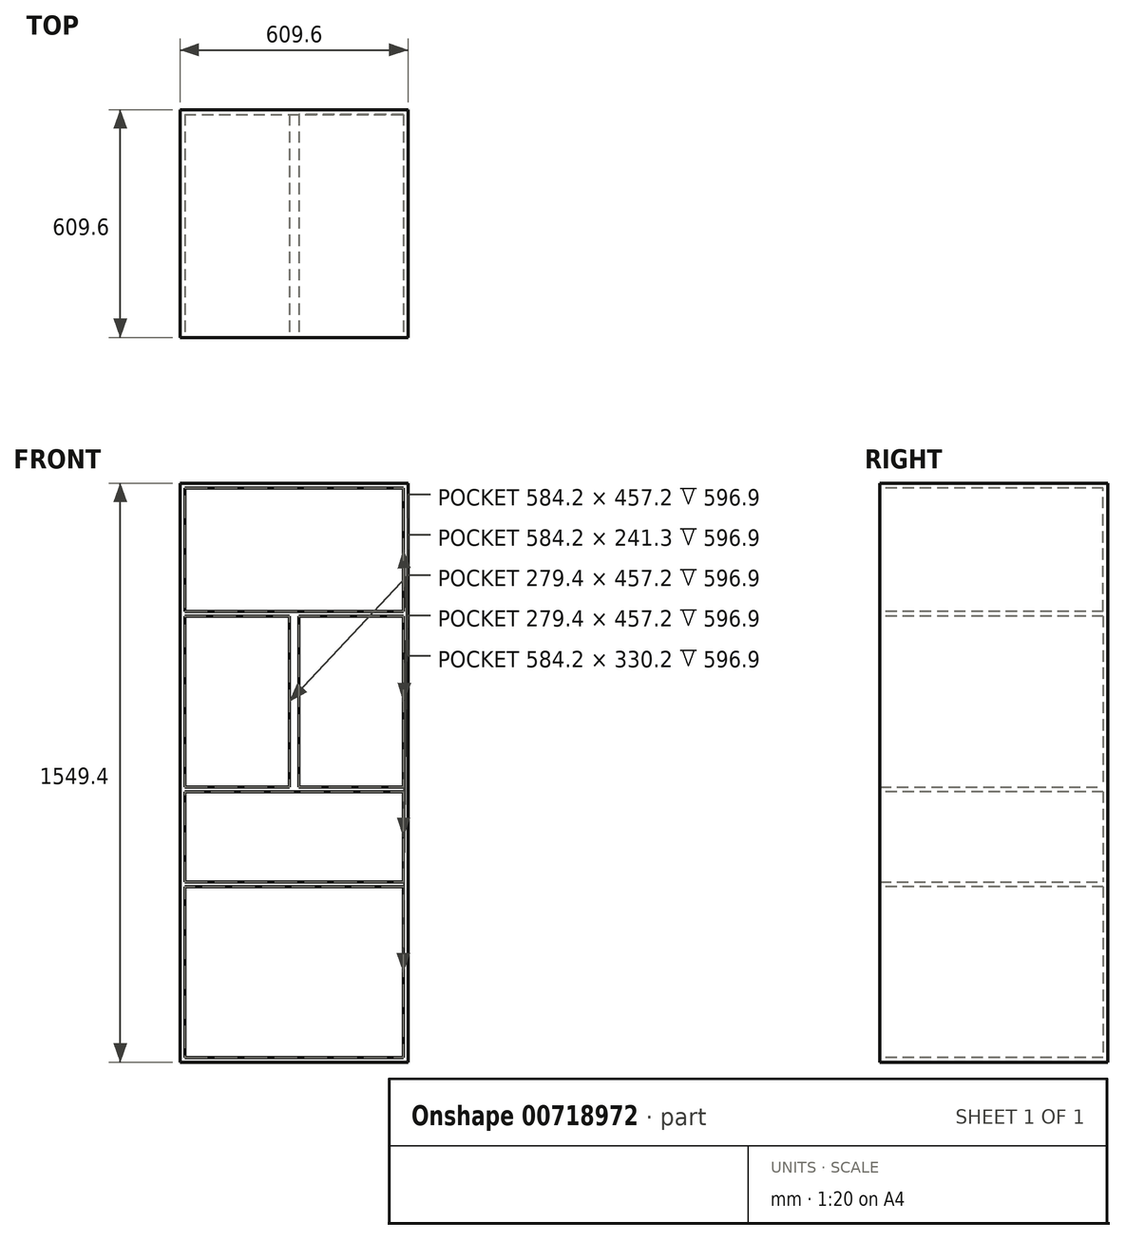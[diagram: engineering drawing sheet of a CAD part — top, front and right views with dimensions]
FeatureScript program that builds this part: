
annotation { "Feature Type Name" : "Feature", "Feature Type Description" : "" }
export const myFeature = defineFeature(function(context is Context, id is Id, definition is map)
    precondition{}
    {
        {
            var Q0;
            Q0=qCreatedBy(makeId("Top.planeOp"),FACE);
            var sketch = newSketch(context, id + "F0", { "sketchPlane" : qUnion([Q0])});
            skLineSegment(sketch, "E0.bottom", {"start": v(-300.8, 335.67) * mm, "end": v(308.8, 335.67) * mm});
            skLineSegment(sketch, "E0.top", {"start": v(-300.8, -273.93) * mm, "end": v(308.8, -273.93) * mm});
            skLineSegment(sketch, "E0.left", {"start": v(-300.8, 335.67) * mm, "end": v(-300.8, -273.93) * mm});
            skLineSegment(sketch, "E0.right", {"start": v(308.8, 335.67) * mm, "end": v(308.8, -273.93) * mm});
            skSolve(sketch);
        }
        {
            var Q0;
            Q0=makeQuery(id+"F0.imprint","IMPRINT",FACE,{"disambiguationData":[TD([[makeQuery(id+"F0.imprint","IMPRINT",EDGE,{"derivedFrom":sQuery(id+"F0.wireOp",EDGE,"E0.bottom")}),-1.0]])]});
            extrude(context, id + "F1", {"entities" : qUnion([Q0]), "depth" : 482.6 * mm, "offsetDistance" : 25.4 * mm});
        }
        {
            var Q0;
            Q0=makeQuery(id+"F1.opExtrude","SWEPT_FACE",FACE,{"disambiguationData":[OSD([sQuery(id+"F0.wireOp",EDGE,"E0.top")])]});
            shell(context, id + "F2", {"entities" : qUnion([Q0]), "thickness" : 12.7 * mm});
        }
        {
            var Q0;
            Q0=makeQuery(id+"F1.opExtrude","CAP_FACE",FACE,{"disambiguationData":[OSD([sQuery(id+"F0.wireOp",EDGE,"E0.bottom"),sQuery(id+"F0.wireOp",EDGE,"E0.top"),sQuery(id+"F0.wireOp",EDGE,"E0.left"),sQuery(id+"F0.wireOp",EDGE,"E0.right")])],"isStart":false});
            extrude(context, id + "F3", {"entities" : qUnion([Q0]), "operationType" : NewBodyOperationType.ADD, "depth" : 254 * mm, "offsetDistance" : 25.4 * mm});
        }
        {
            var Q0;
            {var subQ0=sQuery(id+"F0.wireOp",EDGE,"E0.top");Q0=makeQuery(id+"F3.boolean.opBoolean","MERGE",FACE,{"derivedFrom":[makeQuery(id+"F1.opExtrude","SWEPT_FACE",FACE,{"disambiguationData":[OSD([subQ0])]}),makeQuery(id+"F3.opExtrude","SWEPT_FACE",FACE,{"disambiguationData":[OSD([subQ0])]})]});}
            shell(context, id + "F4", {"entities" : qUnion([Q0]), "thickness" : 12.7 * mm});
        }
        {
            var Q0;
            Q0=makeQuery(id+"F3.opExtrude","CAP_FACE",FACE,{"disambiguationData":[OSD([sQuery(id+"F0.wireOp",EDGE,"E0.bottom"),sQuery(id+"F0.wireOp",EDGE,"E0.top"),sQuery(id+"F0.wireOp",EDGE,"E0.left"),sQuery(id+"F0.wireOp",EDGE,"E0.right")])],"isStart":false});
            var sketch = newSketch(context, id + "F5", { "sketchPlane" : qUnion([Q0])});
            skLineSegment(sketch, "E1.bottom", {"start": v(-300.8, 335.67) * mm, "end": v(4, 335.67) * mm});
            skLineSegment(sketch, "E1.top", {"start": v(-300.8, -273.93) * mm, "end": v(4, -273.93) * mm});
            skLineSegment(sketch, "E1.left", {"start": v(-300.8, 335.67) * mm, "end": v(-300.8, -273.93) * mm});
            skLineSegment(sketch, "E1.right", {"start": v(4, 335.67) * mm, "end": v(4, -273.93) * mm});
            skSolve(sketch);
        }
        {
            var Q0;
            Q0=makeQuery(id+"F5.imprint","IMPRINT",FACE,{"disambiguationData":[TD([[makeQuery(id+"F5.imprint","IMPRINT",EDGE,{"derivedFrom":sQuery(id+"F5.wireOp",EDGE,"E1.bottom")}),-1.0]])]});
            extrude(context, id + "F6", {"entities" : qUnion([Q0]), "operationType" : NewBodyOperationType.ADD, "depth" : 469.9 * mm, "offsetDistance" : 25.4 * mm});
        }
        {
            var Q0;
            {var subQ0=sQuery(id+"F0.wireOp",EDGE,"E0.top");Q0=makeQuery(id+"F6.boolean.opBoolean","MERGE",FACE,{"derivedFrom":[makeQuery(id+"F3.boolean.opBoolean","MERGE",FACE,{"derivedFrom":[makeQuery(id+"F1.opExtrude","SWEPT_FACE",FACE,{"disambiguationData":[OSD([subQ0])]}),makeQuery(id+"F3.opExtrude","SWEPT_FACE",FACE,{"disambiguationData":[OSD([subQ0])]})]}),makeQuery(id+"F6.opExtrude","SWEPT_FACE",FACE,{"disambiguationData":[OSD([sQuery(id+"F5.wireOp",EDGE,"E1.top")])]})]});}
            shell(context, id + "F7", {"entities" : qUnion([Q0]), "thickness" : 12.7 * mm});
        }
        {
            var Q0;
            Q0=makeQuery(id+"F3.opExtrude","CAP_FACE",FACE,{"disambiguationData":[OSD([sQuery(id+"F0.wireOp",EDGE,"E0.bottom"),sQuery(id+"F0.wireOp",EDGE,"E0.top"),sQuery(id+"F0.wireOp",EDGE,"E0.left"),sQuery(id+"F0.wireOp",EDGE,"E0.right")])],"isStart":false});
            extrude(context, id + "F8", {"entities" : qUnion([Q0]), "operationType" : NewBodyOperationType.ADD, "depth" : 469.9 * mm, "offsetDistance" : 25.4 * mm});
        }
        {
            var Q0;
            Q0=makeQuery(id+"F8.boolean.opBoolean","MERGE",FACE,{"derivedFrom":[makeQuery(id+"F6.opExtrude","CAP_FACE",FACE,{"disambiguationData":[OSD([sQuery(id+"F5.wireOp",EDGE,"E1.bottom"),sQuery(id+"F5.wireOp",EDGE,"E1.top"),sQuery(id+"F5.wireOp",EDGE,"E1.left"),sQuery(id+"F5.wireOp",EDGE,"E1.right")])],"isStart":false}),makeQuery(id+"F8.opExtrude","CAP_FACE",FACE,{"disambiguationData":[OSD([sQuery(id+"F0.wireOp",EDGE,"E0.bottom"),sQuery(id+"F0.wireOp",EDGE,"E0.top"),sQuery(id+"F0.wireOp",EDGE,"E0.left"),sQuery(id+"F0.wireOp",EDGE,"E0.right")])],"isStart":false})]});
            extrude(context, id + "F9", {"entities" : qUnion([Q0]), "operationType" : NewBodyOperationType.ADD, "depth" : 342.9 * mm, "offsetDistance" : 25.4 * mm});
        }
        {
            var Q0;
            {var subQ0=sQuery(id+"F5.wireOp",EDGE,"E1.top");var subQ1=sQuery(id+"F0.wireOp",EDGE,"E0.top");Q0=makeQuery(id+"F9.boolean.opBoolean","MERGE",FACE,{"derivedFrom":[makeQuery(id+"F8.boolean.opBoolean","MERGE",FACE,{"derivedFrom":[makeQuery(id+"F6.boolean.opBoolean","MERGE",FACE,{"derivedFrom":[makeQuery(id+"F3.boolean.opBoolean","MERGE",FACE,{"derivedFrom":[makeQuery(id+"F1.opExtrude","SWEPT_FACE",FACE,{"disambiguationData":[OSD([subQ1])]}),makeQuery(id+"F3.opExtrude","SWEPT_FACE",FACE,{"disambiguationData":[OSD([subQ1])]})]}),makeQuery(id+"F6.opExtrude","SWEPT_FACE",FACE,{"disambiguationData":[OSD([subQ0])]})]}),makeQuery(id+"F8.opExtrude","SWEPT_FACE",FACE,{"disambiguationData":[OSD([subQ1])]})]}),makeQuery(id+"F9.opExtrude","SWEPT_FACE",FACE,{"disambiguationData":[OSD([subQ1,subQ0])]})]});}
            var sketch = newSketch(context, id + "F10", { "sketchPlane" : qUnion([Q0])});
            skLineSegment(sketch, "E2.bottom", {"start": v(296.1, 736.6) * mm, "end": v(16.7, 736.6) * mm});
            skLineSegment(sketch, "E2.top", {"start": v(296.1, 1193.8) * mm, "end": v(16.7, 1193.8) * mm});
            skLineSegment(sketch, "E2.left", {"start": v(296.1, 736.6) * mm, "end": v(296.1, 1193.8) * mm});
            skLineSegment(sketch, "E2.right", {"start": v(16.7, 736.6) * mm, "end": v(16.7, 1193.8) * mm});
            skLineSegment(sketch, "E3", {"start": v(-8.7, 1193.8) * mm, "end": v(16.7, 1193.8) * mm});
            skSolve(sketch);
        }
        {
            var Q0;
            Q0=makeQuery(id+"F10.imprint","IMPRINT",FACE,{"disambiguationData":[TD([[makeQuery(id+"F10.imprint","IMPRINT",EDGE,{"derivedFrom":sQuery(id+"F10.wireOp",EDGE,"E2.bottom")}),-1.0]])]});
            extrude(context, id + "F11", {"entities" : qUnion([Q0]), "operationType" : NewBodyOperationType.REMOVE, "oppositeDirection" : true, "depth" : 596.9 * mm, "offsetDistance" : 25.4 * mm});
        }
        {
            var Q0;
            {var subQ0=sQuery(id+"F5.wireOp",EDGE,"E1.top");var subQ1=sQuery(id+"F0.wireOp",EDGE,"E0.top");Q0=makeQuery(id+"F9.boolean.opBoolean","MERGE",FACE,{"derivedFrom":[makeQuery(id+"F8.boolean.opBoolean","MERGE",FACE,{"derivedFrom":[makeQuery(id+"F6.boolean.opBoolean","MERGE",FACE,{"derivedFrom":[makeQuery(id+"F3.boolean.opBoolean","MERGE",FACE,{"derivedFrom":[makeQuery(id+"F1.opExtrude","SWEPT_FACE",FACE,{"disambiguationData":[OSD([subQ1])]}),makeQuery(id+"F3.opExtrude","SWEPT_FACE",FACE,{"disambiguationData":[OSD([subQ1])]})]}),makeQuery(id+"F6.opExtrude","SWEPT_FACE",FACE,{"disambiguationData":[OSD([subQ0])]})]}),makeQuery(id+"F8.opExtrude","SWEPT_FACE",FACE,{"disambiguationData":[OSD([subQ1])]})]}),makeQuery(id+"F9.opExtrude","SWEPT_FACE",FACE,{"disambiguationData":[OSD([subQ1,subQ0])]})]});}
            var sketch = newSketch(context, id + "F12", { "sketchPlane" : qUnion([Q0])});
            skLineSegment(sketch, "E4.bottom", {"start": v(-288.1, 1206.5) * mm, "end": v(296.1, 1206.5) * mm});
            skLineSegment(sketch, "E4.top", {"start": v(-288.1, 1536.7) * mm, "end": v(296.1, 1536.7) * mm});
            skLineSegment(sketch, "E4.left", {"start": v(-288.1, 1206.5) * mm, "end": v(-288.1, 1536.7) * mm});
            skLineSegment(sketch, "E4.right", {"start": v(296.1, 1206.5) * mm, "end": v(296.1, 1536.7) * mm});
            skLineSegment(sketch, "E5", {"start": v(296.1, 1193.8) * mm, "end": v(296.1, 1206.5) * mm});
            skSolve(sketch);
        }
        {
            var Q0;
            Q0=makeQuery(id+"F12.imprint","IMPRINT",FACE,{"disambiguationData":[TD([[makeQuery(id+"F12.imprint","IMPRINT",EDGE,{"derivedFrom":sQuery(id+"F12.wireOp",EDGE,"E4.bottom")}),1.0]])]});
            extrude(context, id + "F13", {"entities" : qUnion([Q0]), "operationType" : NewBodyOperationType.REMOVE, "oppositeDirection" : true, "depth" : 596.9 * mm, "offsetDistance" : 25.4 * mm});
        }
        {
            var Q0;
            {var subQ0=sQuery(id+"F5.wireOp",EDGE,"E1.top");var subQ1=sQuery(id+"F0.wireOp",EDGE,"E0.top");Q0=makeQuery(id+"F9.boolean.opBoolean","MERGE",FACE,{"derivedFrom":[makeQuery(id+"F8.boolean.opBoolean","MERGE",FACE,{"derivedFrom":[makeQuery(id+"F6.boolean.opBoolean","MERGE",FACE,{"derivedFrom":[makeQuery(id+"F3.boolean.opBoolean","MERGE",FACE,{"derivedFrom":[makeQuery(id+"F1.opExtrude","SWEPT_FACE",FACE,{"disambiguationData":[OSD([subQ1])]}),makeQuery(id+"F3.opExtrude","SWEPT_FACE",FACE,{"disambiguationData":[OSD([subQ1])]})]}),makeQuery(id+"F6.opExtrude","SWEPT_FACE",FACE,{"disambiguationData":[OSD([subQ0])]})]}),makeQuery(id+"F8.opExtrude","SWEPT_FACE",FACE,{"disambiguationData":[OSD([subQ1])]})]}),makeQuery(id+"F9.opExtrude","SWEPT_FACE",FACE,{"disambiguationData":[OSD([subQ1,subQ0])]})]});}
            var sketch = newSketch(context, id + "F14", { "sketchPlane" : qUnion([Q0])});
            skLineSegment(sketch, "E6.bottom", {"start": v(-300.8, 1549.4) * mm, "end": v(308.8, 1549.4) * mm});
            skLineSegment(sketch, "E6.top", {"start": v(-300.8, 0) * mm, "end": v(308.8, 0) * mm});
            skLineSegment(sketch, "E6.left", {"start": v(-300.8, 1549.4) * mm, "end": v(-300.8, 0) * mm});
            skLineSegment(sketch, "E6.right", {"start": v(308.8, 1549.4) * mm, "end": v(308.8, 0) * mm});
            skSolve(sketch);
        }
        {
            var Q0;
            Q0 = qSketchRegion(id + "F14", true);
            extrude(context, id + "F15", {"entities" : qUnion([Q0]), "depth" : 12.7 * mm, "offsetDistance" : 25.4 * mm});
        }
        {
            var Q0;
            Q0=makeQuery(id+"F15.opExtrude","SWEPT_BODY",BODY,{"disambiguationData":[OSD([sQuery(id+"F14.wireOp",EDGE,"E6.bottom"),sQuery(id+"F14.wireOp",EDGE,"E6.top"),sQuery(id+"F14.wireOp",EDGE,"E6.left"),sQuery(id+"F14.wireOp",EDGE,"E6.right")])]});
            deleteBodies(context, id + "F16", {"entities" : qUnion([Q0])});
        }
    });
